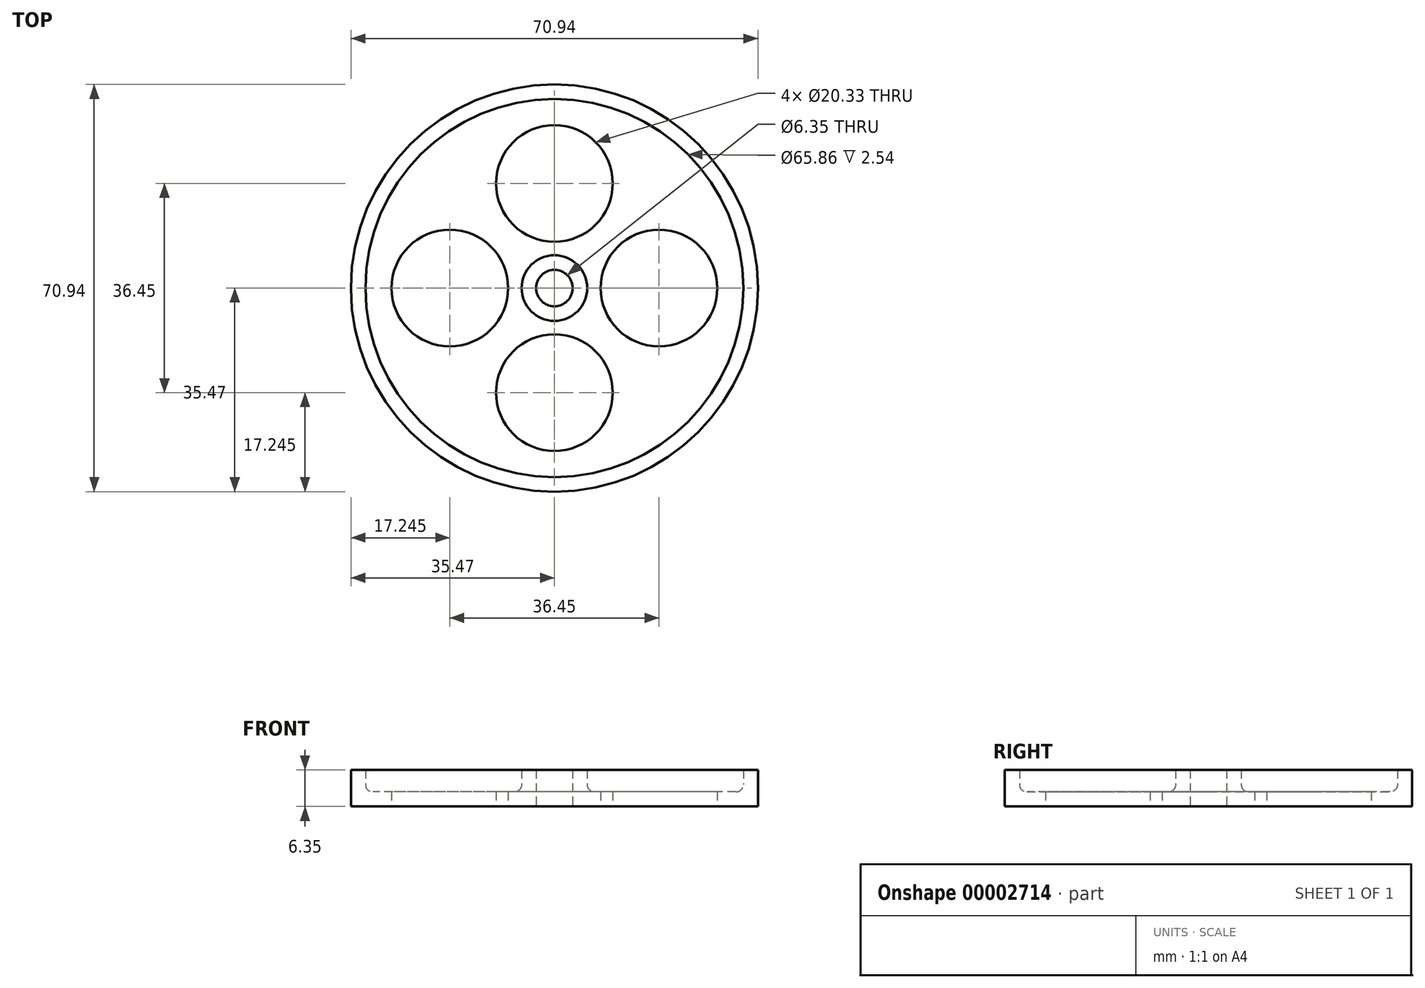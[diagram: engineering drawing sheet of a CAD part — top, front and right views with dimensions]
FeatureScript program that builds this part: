
annotation { "Feature Type Name" : "Feature", "Feature Type Description" : "" }
export const myFeature = defineFeature(function(context is Context, id is Id, definition is map)
    precondition{}
    {
        {
            var Q0;
            Q0=qCreatedBy(makeId("Top.planeOp"),FACE);
            var sketch = newSketch(context, id + "F0", { "sketchPlane" : qUnion([Q0])});
            skCircle(sketch, "E0", {"center": v(0, 0) * mm, "radius": 35.47 * mm});
            skSolve(sketch);
        }
        {
            var Q0;
            Q0=makeQuery(id+"F0.imprint","IMPRINT",FACE,{"disambiguationData":[TD([[makeQuery(id+"F0.imprint","IMPRINT",EDGE,{"derivedFrom":sQuery(id+"F0.wireOp",EDGE,"E0")}),1.0]])]});
            extrude(context, id + "F1", {"entities" : qUnion([Q0]), "depth" : 6.35 * mm});
        }
        {
            var Q0;
            Q0=qCreatedBy(makeId("Top.planeOp"),FACE);
            var sketch = newSketch(context, id + "F2", { "sketchPlane" : qUnion([Q0])});
            skCircle(sketch, "E1", {"center": v(0, 0) * mm, "radius": 3.18 * mm});
            skSolve(sketch);
        }
        {
            var Q0;
            Q0=makeQuery(id+"F2.imprint","IMPRINT",FACE,{"disambiguationData":[TD([[makeQuery(id+"F2.imprint","IMPRINT",EDGE,{"derivedFrom":sQuery(id+"F2.wireOp",EDGE,"E1")}),1.0]])]});
            extrude(context, id + "F3", {"entities" : qUnion([Q0]), "operationType" : NewBodyOperationType.REMOVE, "depth" : 25.4 * mm});
        }
        {
            var Q0;
            Q0=makeQuery(id+"F1.opExtrude","CAP_FACE",FACE,{"disambiguationData":[OSD([sQuery(id+"F0.wireOp",EDGE,"E0")])],"isStart":false});
            shell(context, id + "F4", {"entities" : qUnion([Q0]), "thickness" : 2.54 * mm});
        }
        {
            var Q0;
            {var subQ0=sQuery(id+"F0.wireOp",EDGE,"E0");Q0=makeQuery(id+"F4.opShell","OFFSET_FACE",FACE,{"disambiguationData":[OSD([subQ0]),TDD([makeQuery(id+"F1.opExtrude","CAP_FACE",FACE,{"disambiguationData":[OSD([subQ0])],"isStart":true})])]});}
            var Q1;
            {var subQ0=sQuery(id+"F0.wireOp",EDGE,"E0");Q1=makeQuery(id+"F4.opShell","OFFSET_EDGE",EDGE,{"disambiguationData":[OSD([subQ0]),TDD([makeQuery(id+"F1.opExtrude","CAP_EDGE",EDGE,{"disambiguationData":[OSD([subQ0])],"isStart":true})])]});}
            fillet(context, id + "F5", {"entities" : qUnion([Q0, Q1]), "radius" : 1.27 * mm, "tangentPropagation" : true, "allowEdgeOverflow" : false});
        }
        {
            var Q0;
            Q0=qCreatedBy(makeId("Right.planeOp"),FACE);
            var sketch = newSketch(context, id + "F6", { "sketchPlane" : qUnion([Q0])});
            skArc(sketch, "E2", {"start": v(-35.42, 6.33) * mm, "mid": v(-36, 3.16) * mm, "end": v(-35.41, 0) * mm});
            skSolve(sketch);
        }
        {
            var Q0;
            Q0=qCreatedBy(makeId("Top.planeOp"),FACE);
            var sketch = newSketch(context, id + "F7", { "sketchPlane" : qUnion([Q0])});
            skCircle(sketch, "E3", {"center": v(0, -18.22) * mm, "radius": 10.17 * mm});
            skSolve(sketch);
        }
        {
            var Q0;
            Q0=makeQuery(id+"F7.imprint","IMPRINT",FACE,{"disambiguationData":[TD([[makeQuery(id+"F7.imprint","IMPRINT",EDGE,{"derivedFrom":sQuery(id+"F7.wireOp",EDGE,"E3")}),1.0]])]});
            extrude(context, id + "F8", {"entities" : qUnion([Q0]), "depth" : 25.4 * mm});
        }
        {
            var Q0;
            Q0=makeQuery(id+"F8.opExtrude","SWEPT_BODY",BODY,{"disambiguationData":[OSD([sQuery(id+"F7.wireOp",EDGE,"E3")])]});
            var Q1;
            {var subQ0=sQuery(id+"F0.wireOp",EDGE,"E0");Q1=makeQuery(id+"F5.opFillet","BLEND_EDGE",EDGE,{"blendedFrom":[makeQuery(id+"F4.opShell","OFFSET_EDGE",EDGE,{"disambiguationData":[OSD([sQuery(id+"F2.wireOp",EDGE,"E1")])]}),makeQuery(id+"F4.opShell","OFFSET_FACE",FACE,{"disambiguationData":[OSD([subQ0]),TDD([makeQuery(id+"F1.opExtrude","CAP_FACE",FACE,{"disambiguationData":[OSD([subQ0])],"isStart":true})])]})],"blendedInto":[makeQuery(id+"F4.opShell","OFFSET_FACE",FACE,{"disambiguationData":[OSD([subQ0]),TDD([makeQuery(id+"F1.opExtrude","CAP_FACE",FACE,{"disambiguationData":[OSD([subQ0])],"isStart":true})])]})]});}
            circularPattern(context, id + "F9", {"entities" : qUnion([Q0]), "axis" : qUnion([Q1]), "angle" : 90 * degree, "instanceCount" : 4});
        }
        {
            var Q0;
            Q0=makeQuery(id+"F9.opPattern","COPY",BODY,{"derivedFrom":makeQuery(id+"F8.opExtrude","SWEPT_BODY",BODY,{"disambiguationData":[OSD([sQuery(id+"F7.wireOp",EDGE,"E3")])]}),"instanceName":"1"});
            var Q1;
            Q1=makeQuery(id+"F8.opExtrude","SWEPT_BODY",BODY,{"disambiguationData":[OSD([sQuery(id+"F7.wireOp",EDGE,"E3")])]});
            var Q2;
            Q2=makeQuery(id+"F9.opPattern","COPY",BODY,{"derivedFrom":makeQuery(id+"F8.opExtrude","SWEPT_BODY",BODY,{"disambiguationData":[OSD([sQuery(id+"F7.wireOp",EDGE,"E3")])]}),"instanceName":"3"});
            var Q3;
            Q3=makeQuery(id+"F9.opPattern","COPY",BODY,{"derivedFrom":makeQuery(id+"F8.opExtrude","SWEPT_BODY",BODY,{"disambiguationData":[OSD([sQuery(id+"F7.wireOp",EDGE,"E3")])]}),"instanceName":"2"});
            var Q4;
            Q4=makeQuery(id+"F1.opExtrude","SWEPT_BODY",BODY,{"disambiguationData":[OSD([sQuery(id+"F0.wireOp",EDGE,"E0")])]});
            booleanBodies(context, id + "F10", {"operationType" : BooleanOperationType.SUBTRACTION, "tools" : qUnion([Q0, Q1, Q2, Q3]), "targets" : qUnion([Q4])});
        }
    });
